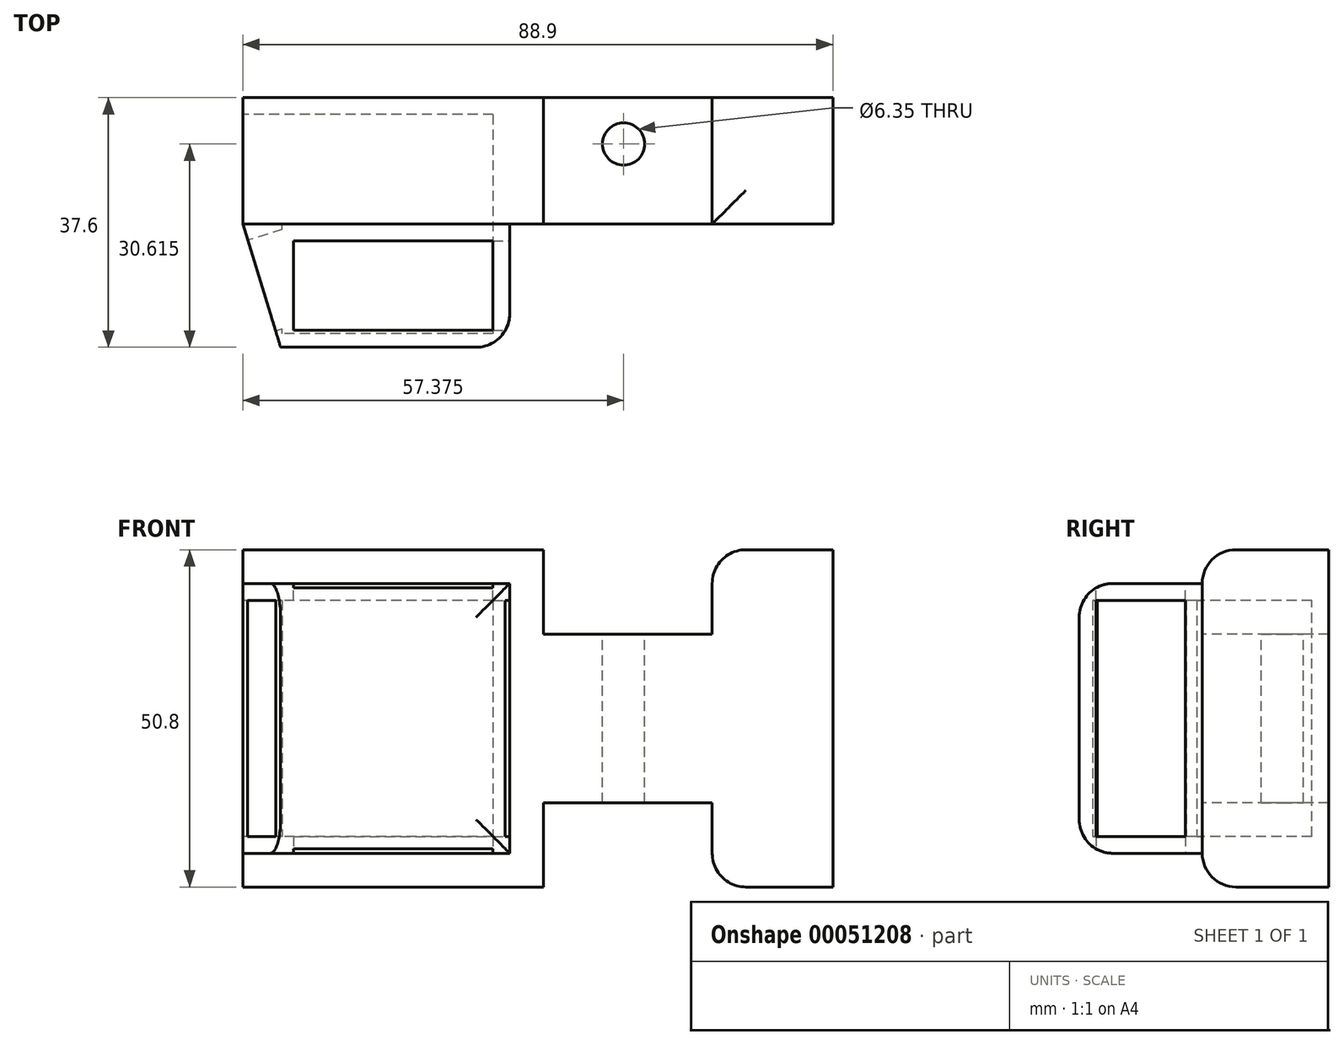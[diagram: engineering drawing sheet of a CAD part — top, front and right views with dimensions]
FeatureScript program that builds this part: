
annotation { "Feature Type Name" : "Feature", "Feature Type Description" : "" }
export const myFeature = defineFeature(function(context is Context, id is Id, definition is map)
    precondition{}
    {
        {
            var Q0;
            Q0=qCreatedBy(makeId("Front.planeOp"),FACE);
            var sketch = newSketch(context, id + "F0", { "sketchPlane" : qUnion([Q0])});
            skLineSegment(sketch, "E0.bottom", {"start": v(0, 0) * mm, "end": v(88.9, 0) * mm});
            skLineSegment(sketch, "E0.top", {"start": v(0, 25.4) * mm, "end": v(88.9, 25.4) * mm});
            skLineSegment(sketch, "E0.left", {"start": v(0, 0) * mm, "end": v(0, 25.4) * mm});
            skLineSegment(sketch, "E0.right", {"start": v(88.9, 0) * mm, "end": v(88.9, 25.4) * mm});
            skSolve(sketch);
        }
        {
            var Q0;
            Q0=qSketchRegion(id+"F0",true);
            extrude(context, id + "F1", {"entities" : qUnion([Q0]), "depth" : 19.05 * mm});
        }
        {
            var Q0;
            Q0=makeQuery(id+"F1.opExtrude","SWEPT_FACE",FACE,{"disambiguationData":[OSD([sQuery(id+"F0.wireOp",EDGE,"E0.top")])]});
            var sketch = newSketch(context, id + "F2", { "sketchPlane" : qUnion([Q0])});
            skLineSegment(sketch, "E1.bottom", {"start": v(70.71, 0) * mm, "end": v(45.31, 0) * mm});
            skLineSegment(sketch, "E1.top", {"start": v(70.71, -19.05) * mm, "end": v(45.31, -19.05) * mm});
            skLineSegment(sketch, "E1.left", {"start": v(70.71, 0) * mm, "end": v(70.71, -19.05) * mm});
            skLineSegment(sketch, "E1.right", {"start": v(45.31, 0) * mm, "end": v(45.31, -19.05) * mm});
            skSolve(sketch);
        }
        {
            var Q0;
            Q0=makeQuery(id+"F2.imprint","IMPRINT",FACE,{"disambiguationData":[TD([[makeQuery(id+"F2.imprint","IMPRINT",EDGE,{"derivedFrom":sQuery(id+"F2.wireOp",EDGE,"E1.bottom")}),-1.0]])]});
            extrude(context, id + "F3", {"entities" : qUnion([Q0]), "operationType" : NewBodyOperationType.REMOVE, "oppositeDirection" : true, "depth" : 12.7 * mm});
        }
        {
            var Q0;
            Q0=makeQuery(id+"F3.boolean.opBoolean","COPY",FACE,{"derivedFrom":makeQuery(id+"F3.opExtrude","CAP_FACE",FACE,{"disambiguationData":[OSD([sQuery(id+"F2.wireOp",EDGE,"E1.bottom"),sQuery(id+"F2.wireOp",EDGE,"E1.top"),sQuery(id+"F2.wireOp",EDGE,"E1.left"),sQuery(id+"F2.wireOp",EDGE,"E1.right")])],"isStart":false})});
            var sketch = newSketch(context, id + "F4", { "sketchPlane" : qUnion([Q0])});
            skCircle(sketch, "E2", {"center": v(57.38, -6.99) * mm, "radius": 3.18 * mm});
            skSolve(sketch);
        }
        {
            var Q0;
            Q0=qSketchRegion(id+"F4",true);
            extrude(context, id + "F5", {"entities" : qUnion([Q0]), "operationType" : NewBodyOperationType.REMOVE, "oppositeDirection" : true, "depth" : 12.7 * mm});
        }
        {
            var Q0;
            Q0=makeQuery(id+"F1.opExtrude","SWEPT_BODY",BODY,{"disambiguationData":[OSD([sQuery(id+"F0.wireOp",EDGE,"E0.bottom"),sQuery(id+"F0.wireOp",EDGE,"E0.top"),sQuery(id+"F0.wireOp",EDGE,"E0.left"),sQuery(id+"F0.wireOp",EDGE,"E0.right")])]});
            var Q1;
            Q1=qCreatedBy(makeId("Top.planeOp"),FACE);
            mirror(context, id + "F6", {"operationType" : NewBodyOperationType.ADD, "entities" : qUnion([Q0]), "mirrorPlane" : qUnion([Q1])});
        }
        {
            var Q0;
            {var subQ0=sQuery(id+"F0.wireOp",EDGE,"E0.left");var subQ1=sQuery(id+"F0.wireOp",EDGE,"E0.top");Q0=makeQuery(id+"F6.opPattern","COPY",EDGE,{"derivedFrom":makeQuery(id+"F3.boolean.opBoolean","SPLIT",EDGE,{"disambiguationData":[TD([makeQuery(id+"F1.opExtrude","SWEPT_FACE",FACE,{"disambiguationData":[OSD([subQ0])]})])],"derivedFrom":makeQuery(id+"F1.opExtrude","CAP_EDGE",EDGE,{"disambiguationData":[OSD([subQ1])],"isStart":false})}),"instanceName":"1"});}
            var Q1;
            {var subQ0=sQuery(id+"F0.wireOp",EDGE,"E0.left");var subQ1=sQuery(id+"F0.wireOp",EDGE,"E0.top");Q1=makeQuery(id+"F3.boolean.opBoolean","SPLIT",EDGE,{"disambiguationData":[TD([makeQuery(id+"F1.opExtrude","SWEPT_FACE",FACE,{"disambiguationData":[OSD([subQ0])]})])],"derivedFrom":makeQuery(id+"F1.opExtrude","CAP_EDGE",EDGE,{"disambiguationData":[OSD([subQ1])],"isStart":false})});}
            var Q2;
            Q2=makeQuery(id+"F6.opPattern","COPY",EDGE,{"derivedFrom":makeQuery(id+"F3.boolean.opBoolean","COPY",EDGE,{"derivedFrom":makeQuery(id+"F3.opExtrude","CAP_EDGE",EDGE,{"disambiguationData":[OSD([sQuery(id+"F2.wireOp",EDGE,"E1.right")])],"isStart":true})}),"instanceName":"1"});
            var Q3;
            Q3=makeQuery(id+"F6.opPattern","COPY",EDGE,{"derivedFrom":makeQuery(id+"F3.boolean.opBoolean","COPY",EDGE,{"derivedFrom":makeQuery(id+"F3.opExtrude","SWEPT_EDGE",EDGE,{"disambiguationData":[OSD([sQuery(id+"F0.wireOp",EDGE,"E0.top"),sQuery(id+"F2.wireOp",EDGE,"E1.top"),sQuery(id+"F2.wireOp",EDGE,"E1.right")])]})}),"instanceName":"1"});
            var Q4;
            Q4=makeQuery(id+"F6.opPattern","COPY",EDGE,{"derivedFrom":makeQuery(id+"F3.boolean.opBoolean","COPY",EDGE,{"derivedFrom":makeQuery(id+"F3.opExtrude","SWEPT_EDGE",EDGE,{"disambiguationData":[OSD([sQuery(id+"F0.wireOp",EDGE,"E0.top"),sQuery(id+"F2.wireOp",EDGE,"E1.top"),sQuery(id+"F2.wireOp",EDGE,"E1.left")])]})}),"instanceName":"1"});
            var Q5;
            Q5=makeQuery(id+"F6.opPattern","COPY",EDGE,{"derivedFrom":makeQuery(id+"F3.boolean.opBoolean","COPY",EDGE,{"derivedFrom":makeQuery(id+"F3.opExtrude","CAP_EDGE",EDGE,{"disambiguationData":[OSD([sQuery(id+"F2.wireOp",EDGE,"E1.left")])],"isStart":true})}),"instanceName":"1"});
            var Q6;
            Q6=makeQuery(id+"F3.boolean.opBoolean","COPY",EDGE,{"derivedFrom":makeQuery(id+"F3.opExtrude","CAP_EDGE",EDGE,{"disambiguationData":[OSD([sQuery(id+"F2.wireOp",EDGE,"E1.left")])],"isStart":true})});
            var Q7;
            Q7=makeQuery(id+"F3.boolean.opBoolean","COPY",EDGE,{"derivedFrom":makeQuery(id+"F3.opExtrude","SWEPT_EDGE",EDGE,{"disambiguationData":[OSD([sQuery(id+"F0.wireOp",EDGE,"E0.top"),sQuery(id+"F2.wireOp",EDGE,"E1.top"),sQuery(id+"F2.wireOp",EDGE,"E1.left")])]})});
            var Q8;
            Q8=makeQuery(id+"F3.boolean.opBoolean","COPY",EDGE,{"derivedFrom":makeQuery(id+"F3.opExtrude","CAP_EDGE",EDGE,{"disambiguationData":[OSD([sQuery(id+"F2.wireOp",EDGE,"E1.right")])],"isStart":true})});
            var Q9;
            Q9=makeQuery(id+"F3.boolean.opBoolean","COPY",EDGE,{"derivedFrom":makeQuery(id+"F3.opExtrude","SWEPT_EDGE",EDGE,{"disambiguationData":[OSD([sQuery(id+"F0.wireOp",EDGE,"E0.top"),sQuery(id+"F2.wireOp",EDGE,"E1.top"),sQuery(id+"F2.wireOp",EDGE,"E1.right")])]})});
            var Q10;
            Q10=makeQuery(id+"F6.opPattern","COPY",EDGE,{"derivedFrom":makeQuery(id+"F3.boolean.opBoolean","COPY",EDGE,{"derivedFrom":makeQuery(id+"F3.opExtrude","CAP_EDGE",EDGE,{"disambiguationData":[OSD([sQuery(id+"F2.wireOp",EDGE,"E1.top")])],"isStart":false})}),"instanceName":"1"});
            var Q11;
            Q11=makeQuery(id+"F3.boolean.opBoolean","COPY",EDGE,{"derivedFrom":makeQuery(id+"F3.opExtrude","CAP_EDGE",EDGE,{"disambiguationData":[OSD([sQuery(id+"F2.wireOp",EDGE,"E1.top")])],"isStart":false})});
            var Q12;
            {var subQ0=sQuery(id+"F0.wireOp",EDGE,"E0.right");var subQ1=sQuery(id+"F0.wireOp",EDGE,"E0.top");Q12=makeQuery(id+"F6.opPattern","COPY",EDGE,{"derivedFrom":makeQuery(id+"F3.boolean.opBoolean","SPLIT",EDGE,{"disambiguationData":[TD([makeQuery(id+"F1.opExtrude","SWEPT_FACE",FACE,{"disambiguationData":[OSD([subQ0])]})])],"derivedFrom":makeQuery(id+"F1.opExtrude","CAP_EDGE",EDGE,{"disambiguationData":[OSD([subQ1])],"isStart":false})}),"instanceName":"1"});}
            var Q13;
            {var subQ0=sQuery(id+"F0.wireOp",EDGE,"E0.right");var subQ1=sQuery(id+"F0.wireOp",EDGE,"E0.top");Q13=makeQuery(id+"F3.boolean.opBoolean","SPLIT",EDGE,{"disambiguationData":[TD([makeQuery(id+"F1.opExtrude","SWEPT_FACE",FACE,{"disambiguationData":[OSD([subQ0])]})])],"derivedFrom":makeQuery(id+"F1.opExtrude","CAP_EDGE",EDGE,{"disambiguationData":[OSD([subQ1])],"isStart":false})});}
            fillet(context, id + "F7", {"entities" : qUnion([Q0, Q1, Q2, Q3, Q4, Q5, Q6, Q7, Q8, Q9, Q10, Q11, Q12, Q13]), "radius" : 5.08 * mm, "tangentPropagation" : true, "allowEdgeOverflow" : false});
        }
        {
            var Q0;
            {var subQ0=makeQuery(id+"F1.opExtrude","CAP_FACE",FACE,{"disambiguationData":[OSD([sQuery(id+"F0.wireOp",EDGE,"E0.bottom"),sQuery(id+"F0.wireOp",EDGE,"E0.top"),sQuery(id+"F0.wireOp",EDGE,"E0.left"),sQuery(id+"F0.wireOp",EDGE,"E0.right")])],"isStart":false});Q0=makeQuery(id+"F6.boolean.opBoolean","MERGE",FACE,{"derivedFrom":[subQ0,makeQuery(id+"F6.opPattern","COPY",FACE,{"derivedFrom":subQ0,"instanceName":"1"})]});}
            var sketch = newSketch(context, id + "F8", { "sketchPlane" : qUnion([Q0])});
            skLineSegment(sketch, "E3.bottom", {"start": v(37.7, 17.78) * mm, "end": v(0, 17.78) * mm});
            skLineSegment(sketch, "E3.top", {"start": v(37.7, -17.78) * mm, "end": v(0, -17.78) * mm});
            skLineSegment(sketch, "E3.left", {"start": v(37.7, 17.78) * mm, "end": v(37.7, -17.78) * mm});
            skLineSegment(sketch, "E3.right", {"start": v(0, 17.78) * mm, "end": v(0, -17.78) * mm});
            skSolve(sketch);
        }
        {
            var Q0;
            Q0 = qSketchRegion(id + "F8", true);
            extrude(context, id + "F9", {"entities" : qUnion([Q0]), "operationType" : NewBodyOperationType.REMOVE, "oppositeDirection" : true, "depth" : 16.5 * mm});
        }
        {
            var Q0;
            {var subQ0=makeQuery(id+"F1.opExtrude","CAP_FACE",FACE,{"disambiguationData":[OSD([sQuery(id+"F0.wireOp",EDGE,"E0.bottom"),sQuery(id+"F0.wireOp",EDGE,"E0.top"),sQuery(id+"F0.wireOp",EDGE,"E0.left"),sQuery(id+"F0.wireOp",EDGE,"E0.right")])],"isStart":false});Q0=makeQuery(id+"F6.boolean.opBoolean","MERGE",FACE,{"derivedFrom":[subQ0,makeQuery(id+"F6.opPattern","COPY",FACE,{"derivedFrom":subQ0,"instanceName":"1"})]});}
            var sketch = newSketch(context, id + "F10", { "sketchPlane" : qUnion([Q0])});
            skLineSegment(sketch, "E4.bottom", {"start": v(40.23, 20.32) * mm, "end": v(0, 20.32) * mm});
            skLineSegment(sketch, "E4.top", {"start": v(40.23, -20.32) * mm, "end": v(0, -20.32) * mm});
            skLineSegment(sketch, "E4.left", {"start": v(40.23, 20.32) * mm, "end": v(40.23, -20.32) * mm});
            skLineSegment(sketch, "E4.right", {"start": v(0, 20.32) * mm, "end": v(0, -20.32) * mm});
            skSolve(sketch);
        }
        {
            var Q0;
            Q0 = qSketchRegion(id + "F10", true);
            extrude(context, id + "F11", {"entities" : qUnion([Q0]), "operationType" : NewBodyOperationType.ADD, "depth" : 18.55 * mm});
        }
        {
            var Q0;
            Q0=makeQuery(id+"F11.opExtrude","CAP_FACE",FACE,{"disambiguationData":[OSD([sQuery(id+"F10.wireOp",EDGE,"E4.bottom"),sQuery(id+"F10.wireOp",EDGE,"E4.top"),sQuery(id+"F10.wireOp",EDGE,"E4.left"),sQuery(id+"F10.wireOp",EDGE,"E4.right")])],"isStart":true});
            var sketch = newSketch(context, id + "F12", { "sketchPlane" : qUnion([Q0])});
            skLineSegment(sketch, "E5.bottom", {"start": v(-37.7, -17.78) * mm, "end": v(-5.94, -17.78) * mm});
            skLineSegment(sketch, "E5.top", {"start": v(-37.7, 17.78) * mm, "end": v(-5.94, 17.78) * mm});
            skLineSegment(sketch, "E5.left", {"start": v(-37.7, -17.78) * mm, "end": v(-37.7, 17.78) * mm});
            skLineSegment(sketch, "E5.right", {"start": v(-5.94, -17.78) * mm, "end": v(-5.94, 17.78) * mm});
            skSolve(sketch);
        }
        {
            var Q0;
            Q0 = qSketchRegion(id + "F12", true);
            extrude(context, id + "F13", {"entities" : qUnion([Q0]), "operationType" : NewBodyOperationType.REMOVE, "oppositeDirection" : true, "depth" : 16.5 * mm});
        }
        {
            var Q0;
            Q0=makeQuery(id+"F11.opExtrude","SWEPT_FACE",FACE,{"disambiguationData":[OSD([sQuery(id+"F10.wireOp",EDGE,"E4.top")])]});
            var sketch = newSketch(context, id + "F14", { "sketchPlane" : qUnion([Q0])});
            skLineSegment(sketch, "E6.bottom", {"start": v(7.62, 35.06) * mm, "end": v(37.7, 35.06) * mm});
            skLineSegment(sketch, "E6.top", {"start": v(7.62, 21.59) * mm, "end": v(37.7, 21.59) * mm});
            skLineSegment(sketch, "E6.left", {"start": v(7.62, 35.06) * mm, "end": v(7.62, 21.59) * mm});
            skLineSegment(sketch, "E6.right", {"start": v(37.7, 35.06) * mm, "end": v(37.7, 21.59) * mm});
            skSolve(sketch);
        }
        {
            var Q0;
            Q0 = qSketchRegion(id + "F14", true);
            extrude(context, id + "F15", {"entities" : qUnion([Q0]), "operationType" : NewBodyOperationType.REMOVE, "oppositeDirection" : true, "depth" : 2.54 * mm});
        }
        {
            var Q0;
            Q0=makeQuery(id+"F11.opExtrude","SWEPT_FACE",FACE,{"disambiguationData":[OSD([sQuery(id+"F10.wireOp",EDGE,"E4.bottom")])]});
            var sketch = newSketch(context, id + "F16", { "sketchPlane" : qUnion([Q0])});
            skLineSegment(sketch, "E7.bottom", {"start": v(37.7, -35.06) * mm, "end": v(7.62, -35.06) * mm});
            skLineSegment(sketch, "E7.top", {"start": v(37.7, -21.59) * mm, "end": v(7.62, -21.59) * mm});
            skLineSegment(sketch, "E7.left", {"start": v(37.7, -35.06) * mm, "end": v(37.7, -21.59) * mm});
            skLineSegment(sketch, "E7.right", {"start": v(7.62, -35.06) * mm, "end": v(7.62, -21.59) * mm});
            skSolve(sketch);
        }
        {
            var Q0;
            Q0 = qSketchRegion(id + "F16", true);
            extrude(context, id + "F17", {"entities" : qUnion([Q0]), "operationType" : NewBodyOperationType.REMOVE, "oppositeDirection" : true, "depth" : 2.54 * mm});
        }
        {
            var Q0;
            Q0=makeQuery(id+"F11.opExtrude","SWEPT_FACE",FACE,{"disambiguationData":[OSD([sQuery(id+"F10.wireOp",EDGE,"E4.bottom")])]});
            var sketch = newSketch(context, id + "F18", { "sketchPlane" : qUnion([Q0])});
            skLineSegment(sketch, "E8", {"start": v(5.7, -37.6) * mm, "end": v(0, -19.05) * mm});
            skLineSegment(sketch, "E9", {"start": v(0, -19.05) * mm, "end": v(0, -37.6) * mm});
            skLineSegment(sketch, "E10", {"start": v(0, -37.6) * mm, "end": v(5.7, -37.6) * mm});
            skSolve(sketch);
        }
        {
            var Q0;
            Q0 = qSketchRegion(id + "F18", true);
            extrude(context, id + "F19", {"entities" : qUnion([Q0]), "operationType" : NewBodyOperationType.REMOVE, "oppositeDirection" : true, "depth" : 50.8 * mm});
        }
        {
            var Q0;
            Q0=makeQuery(id+"F19.boolean.opBoolean","COPY",FACE,{"derivedFrom":makeQuery(id+"F19.opExtrude","SWEPT_FACE",FACE,{"disambiguationData":[OSD([sQuery(id+"F18.wireOp",EDGE,"E8")])]})});
            var sketch = newSketch(context, id + "F20", { "sketchPlane" : qUnion([Q0])});
            skLineSegment(sketch, "E11.bottom", {"start": v(35.08, 17.78) * mm, "end": v(20.75, 17.78) * mm});
            skLineSegment(sketch, "E11.top", {"start": v(35.08, -17.78) * mm, "end": v(20.75, -17.78) * mm});
            skLineSegment(sketch, "E11.left", {"start": v(35.08, 17.78) * mm, "end": v(35.08, -17.78) * mm});
            skLineSegment(sketch, "E11.right", {"start": v(20.75, 17.78) * mm, "end": v(20.75, -17.78) * mm});
            skSolve(sketch);
        }
        {
            var Q0;
            Q0 = qSketchRegion(id + "F20", true);
            extrude(context, id + "F21", {"entities" : qUnion([Q0]), "operationType" : NewBodyOperationType.REMOVE, "oppositeDirection" : true, "depth" : 7.62 * mm});
        }
        {
            var Q0;
            Q0=makeQuery(id+"F11.opExtrude","SWEPT_FACE",FACE,{"disambiguationData":[OSD([sQuery(id+"F10.wireOp",EDGE,"E4.left")])]});
            var sketch = newSketch(context, id + "F22", { "sketchPlane" : qUnion([Q0])});
            skLineSegment(sketch, "E12.bottom", {"start": v(-35.06, -17.78) * mm, "end": v(-21.59, -17.78) * mm});
            skLineSegment(sketch, "E12.top", {"start": v(-35.06, 17.78) * mm, "end": v(-21.6, 17.78) * mm});
            skLineSegment(sketch, "E12.left", {"start": v(-35.06, -17.78) * mm, "end": v(-35.06, 17.78) * mm});
            skLineSegment(sketch, "E12.right", {"start": v(-21.59, -17.78) * mm, "end": v(-21.59, 17.78) * mm});
            skSolve(sketch);
        }
        {
            var Q0;
            Q0 = qSketchRegion(id + "F22", true);
            extrude(context, id + "F23", {"entities" : qUnion([Q0]), "operationType" : NewBodyOperationType.REMOVE, "oppositeDirection" : true, "depth" : 5.08 * mm});
        }
        {
            var Q0;
            Q0=makeQuery(id+"F19.boolean.opBoolean","COPY",EDGE,{"derivedFrom":makeQuery(id+"F19.opExtrude","SWEPT_EDGE",EDGE,{"disambiguationData":[OSD([sQuery(id+"F10.wireOp",EDGE,"E4.bottom"),sQuery(id+"F18.wireOp",EDGE,"E8"),sQuery(id+"F18.wireOp",EDGE,"E10")])]})});
            var Q1;
            Q1=makeQuery(id+"F11.opExtrude","CAP_EDGE",EDGE,{"disambiguationData":[OSD([sQuery(id+"F10.wireOp",EDGE,"E4.bottom")])],"isStart":false});
            var Q2;
            Q2=makeQuery(id+"F11.opExtrude","CAP_EDGE",EDGE,{"disambiguationData":[OSD([sQuery(id+"F10.wireOp",EDGE,"E4.top")])],"isStart":false});
            var Q3;
            Q3=makeQuery(id+"F11.opExtrude","CAP_EDGE",EDGE,{"disambiguationData":[OSD([sQuery(id+"F10.wireOp",EDGE,"E4.left")])],"isStart":false});
            fillet(context, id + "F24", {"entities" : qUnion([Q0, Q1, Q2, Q3]), "radius" : 5.08 * mm, "tangentPropagation" : true, "allowEdgeOverflow" : false});
        }
    });
